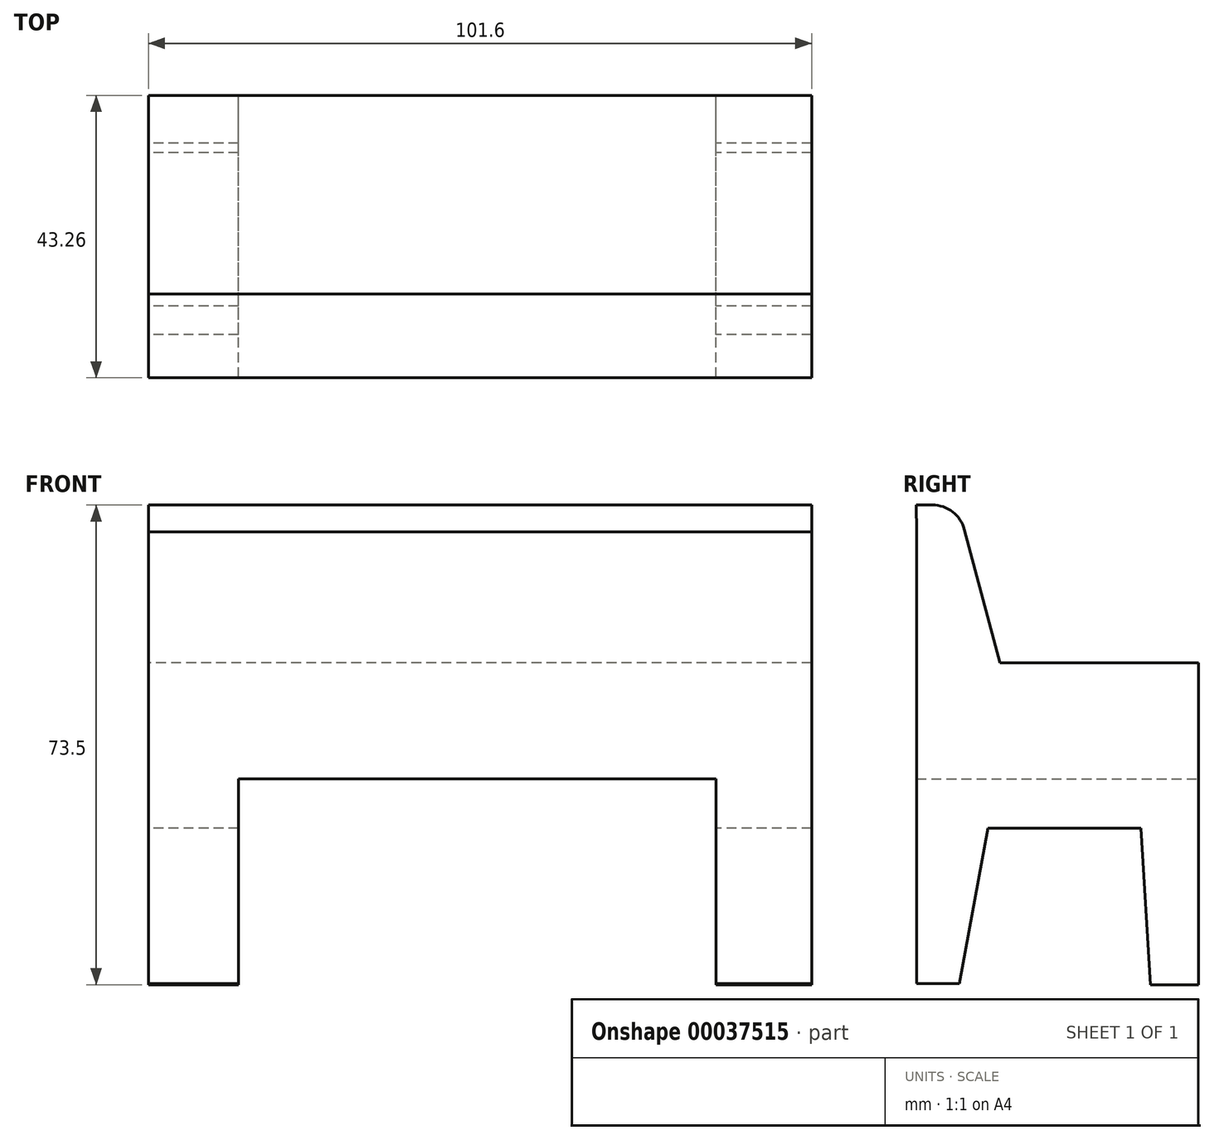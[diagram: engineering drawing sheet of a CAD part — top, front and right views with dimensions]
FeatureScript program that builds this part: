
annotation { "Feature Type Name" : "Feature", "Feature Type Description" : "" }
export const myFeature = defineFeature(function(context is Context, id is Id, definition is map)
    precondition{}
    {
        {
            var Q0;
            Q0=qCreatedBy(makeId("Right.planeOp"),FACE);
            var sketch = newSketch(context, id + "F0", { "sketchPlane" : qUnion([Q0])});
            skLineSegment(sketch, "E0", {"start": v(-66.23, 41.99) * mm, "end": v(-66.23, -27.22) * mm});
            skLineSegment(sketch, "E1", {"start": v(-66.23, -27.22) * mm, "end": v(-59.7, -27.22) * mm});
            skLineSegment(sketch, "E2", {"start": v(-59.7, -27.22) * mm, "end": v(-55.3, -3.4) * mm});
            skLineSegment(sketch, "E3", {"start": v(-55.3, -3.4) * mm, "end": v(-31.84, -3.4) * mm});
            skLineSegment(sketch, "E4", {"start": v(-31.84, -3.4) * mm, "end": v(-30.37, -27.4) * mm});
            skLineSegment(sketch, "E5", {"start": v(-30.37, -27.4) * mm, "end": v(-23.04, -27.4) * mm});
            skLineSegment(sketch, "E6", {"start": v(-23.04, -27.4) * mm, "end": v(-23.04, -3.03) * mm});
            skLineSegment(sketch, "E7", {"start": v(-23.04, -3.03) * mm, "end": v(-23.04, 21.9) * mm});
            skLineSegment(sketch, "E8", {"start": v(-23.04, 21.9) * mm, "end": v(-53.47, 21.9) * mm});
            skLineSegment(sketch, "E9", {"start": v(-53.47, 21.9) * mm, "end": v(-59.89, 46.1) * mm});
            skLineSegment(sketch, "E10", {"start": v(-59.89, 46.1) * mm, "end": v(-66.3, 46.1) * mm});
            skLineSegment(sketch, "E11", {"start": v(-66.3, 46.1) * mm, "end": v(-66.23, 41.99) * mm});
            skSolve(sketch);
        }
        {
            var Q0;
            Q0=makeQuery(id+"F0.imprint","IMPRINT",FACE,{"disambiguationData":[TD([[makeQuery(id+"F0.imprint","IMPRINT",EDGE,{"derivedFrom":sQuery(id+"F0.wireOp",EDGE,"E0")}),1.0]])]});
            extrude(context, id + "F1", {"entities" : qUnion([Q0]), "depth" : 101.6 * mm});
        }
        {
            var Q0;
            Q0=makeQuery(id+"F1.opExtrude","SWEPT_FACE",FACE,{"disambiguationData":[OSD([sQuery(id+"F0.wireOp",EDGE,"E6"),sQuery(id+"F0.wireOp",EDGE,"E7")])]});
            var sketch = newSketch(context, id + "F2", { "sketchPlane" : qUnion([Q0])});
            skLineSegment(sketch, "E12.bottom", {"start": v(-86.94, 4.12) * mm, "end": v(-13.8, 4.12) * mm});
            skLineSegment(sketch, "E12.top", {"start": v(-86.94, -27.4) * mm, "end": v(-13.8, -27.4) * mm});
            skLineSegment(sketch, "E12.left", {"start": v(-86.94, 4.12) * mm, "end": v(-86.94, -27.4) * mm});
            skLineSegment(sketch, "E12.right", {"start": v(-13.8, 4.12) * mm, "end": v(-13.8, -27.4) * mm});
            skSolve(sketch);
        }
        {
            var Q0;
            Q0=makeQuery(id+"F2.imprint","IMPRINT",FACE,{"disambiguationData":[TD([[makeQuery(id+"F2.imprint","IMPRINT",EDGE,{"derivedFrom":sQuery(id+"F2.wireOp",EDGE,"E12.bottom")}),-1.0]])]});
            extrude(context, id + "F3", {"entities" : qUnion([Q0]), "operationType" : NewBodyOperationType.REMOVE, "endBound" : BoundingType.THROUGH_ALL, "oppositeDirection" : true, "depth" : 25.4 * mm});
        }
        {
            var Q0;
            Q0=makeQuery(id+"F1.opExtrude","SWEPT_EDGE",EDGE,{"disambiguationData":[OSD([sQuery(id+"F0.wireOp",EDGE,"E9"),sQuery(id+"F0.wireOp",EDGE,"E10")])]});
            fillet(context, id + "F4", {"entities" : qUnion([Q0]), "radius" : 5.08 * mm, "tangentPropagation" : true, "allowEdgeOverflow" : false});
        }
    });
